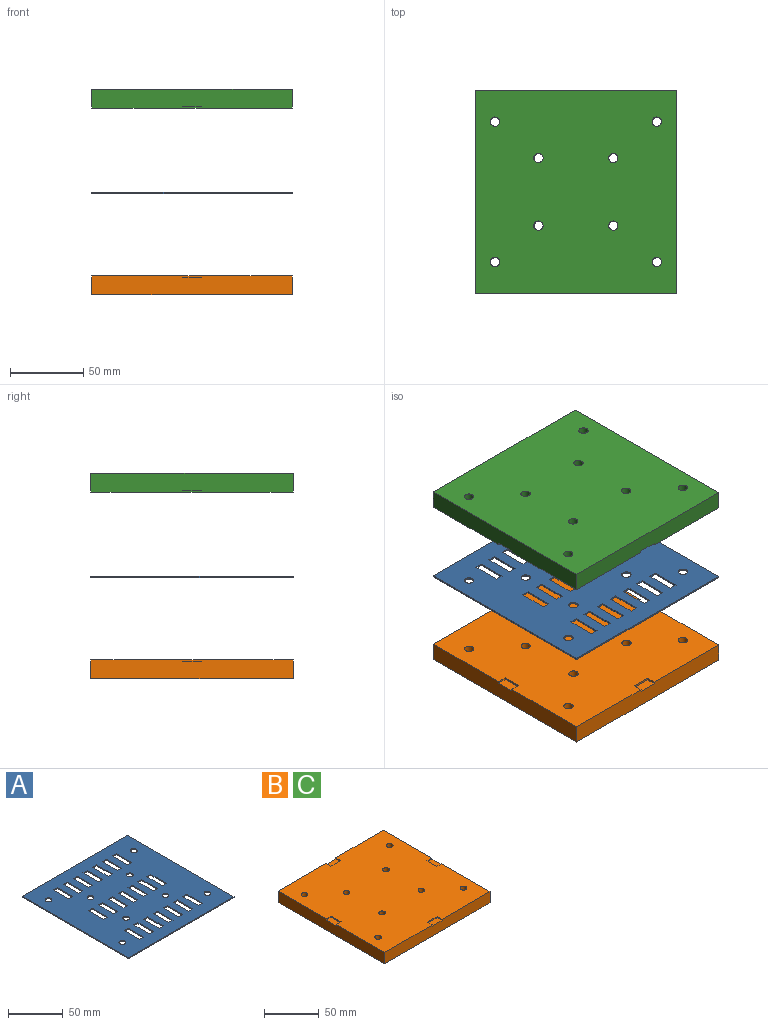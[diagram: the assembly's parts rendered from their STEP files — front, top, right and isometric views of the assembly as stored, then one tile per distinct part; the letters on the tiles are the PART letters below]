
ASSEMBLY  parts=3 mates=2
PART A: 98 faces, bbox 136.8x138x1 mm
  f0: plane 138.04x136.82mm, normal (0,0,1), area 16433.2mm2, adj f2,f3,f4,f5,f6,f7,f8,f9
  f1: plane 138.04x136.82mm, normal (0,0,-1), area 16433.2mm2, adj f2,f3,f4,f5,f6,f7,f8,f9
  f2: plane 138.04x1.02mm, normal (-1,0,0), area 140.3mm2, adj f0,f1,f3,f5
  f3: plane 136.82x1.02mm, normal (0,-1,0), area 139mm2, adj f0,f1,f2,f4
  f4: plane 138.04x1.02mm, normal (1,0,0), area 140.3mm2, adj f0,f1,f3,f5
  f5: plane 136.82x1.02mm, normal (0,1,0), area 139mm2, adj f0,f1,f2,f4
  f6: plane 5.24x1.02mm, normal (0,-1,0), area 5.3mm2, adj f0,f1,f7,f9
  f7: plane 20.02x1.02mm, normal (1,0,0), area 20.3mm2, adj f0,f1,f6,f8
  f8: plane 5.24x1.02mm, normal (0,1,0), area 5.3mm2, adj f0,f1,f7,f9
  f9: plane 20.02x1.02mm, normal (-1,0,0), area 20.3mm2, adj f0,f1,f6,f8
  f10: plane 5.24x1.02mm, normal (0,1,0), area 5.3mm2, adj f0,f1,f11,f12
  f11: plane 20.02x1.02mm, normal (1,0,0), area 20.3mm2, adj f0,f1,f10,f13
  f12: plane 20.02x1.02mm, normal (-1,0,0), area 20.3mm2, adj f0,f1,f10,f13
  f13: plane 5.24x1.02mm, normal (0,-1,0), area 5.3mm2, adj f0,f1,f11,f12
  f14: plane 5.24x1.02mm, normal (0,1,0), area 5.3mm2, adj f0,f1,f15,f16
  f15: plane 20.02x1.02mm, normal (1,0,0), area 20.3mm2, adj f0,f1,f14,f17
  f16: plane 20.02x1.02mm, normal (-1,0,0), area 20.3mm2, adj f0,f1,f14,f17
  f17: plane 5.24x1.02mm, normal (0,-1,0), area 5.3mm2, adj f0,f1,f15,f16
  f18: plane 5.24x1.02mm, normal (0,1,0), area 5.3mm2, adj f0,f1,f19,f20
  f19: plane 20.02x1.02mm, normal (1,0,0), area 20.3mm2, adj f0,f1,f18,f21
  f20: plane 20.02x1.02mm, normal (-1,0,0), area 20.3mm2, adj f0,f1,f18,f21
  f21: plane 5.24x1.02mm, normal (0,-1,0), area 5.3mm2, adj f0,f1,f19,f20
  f22: plane 5.24x1.02mm, normal (0,1,0), area 5.3mm2, adj f0,f1,f23,f24
  f23: plane 20.02x1.02mm, normal (1,0,0), area 20.3mm2, adj f0,f1,f22,f25
  f24: plane 20.02x1.02mm, normal (-1,0,0), area 20.3mm2, adj f0,f1,f22,f25
  f25: plane 5.24x1.02mm, normal (0,-1,0), area 5.3mm2, adj f0,f1,f23,f24
  f26: plane 5.24x1.02mm, normal (0,1,0), area 5.3mm2, adj f0,f1,f27,f28
  f27: plane 20.02x1.02mm, normal (1,0,0), area 20.3mm2, adj f0,f1,f26,f29
  f28: plane 20.02x1.02mm, normal (-1,0,0), area 20.3mm2, adj f0,f1,f26,f29
  f29: plane 5.24x1.02mm, normal (0,-1,0), area 5.3mm2, adj f0,f1,f27,f28
  f30: plane 20.02x1.02mm, normal (-1,0,0), area 20.3mm2, adj f0,f1,f31,f32
  f31: plane 5.24x1.02mm, normal (0,1,0), area 5.3mm2, adj f0,f1,f30,f33
  f32: plane 5.24x1.02mm, normal (0,-1,0), area 5.3mm2, adj f0,f1,f30,f33
  f33: plane 20.02x1.02mm, normal (1,0,0), area 20.3mm2, adj f0,f1,f31,f32
  f34: plane 20.02x1.02mm, normal (-1,0,0), area 20.3mm2, adj f0,f1,f35,f36
  f35: plane 5.24x1.02mm, normal (0,1,0), area 5.3mm2, adj f0,f1,f34,f37
  f36: plane 5.24x1.02mm, normal (0,-1,0), area 5.3mm2, adj f0,f1,f34,f37
  f37: plane 20.02x1.02mm, normal (1,0,0), area 20.3mm2, adj f0,f1,f35,f36
  f38: plane 5.24x1.02mm, normal (0,1,0), area 5.3mm2, adj f0,f1,f39,f40
  f39: plane 20.02x1.02mm, normal (1,0,0), area 20.3mm2, adj f0,f1,f38,f41
  f40: plane 20.02x1.02mm, normal (-1,0,0), area 20.3mm2, adj f0,f1,f38,f41
  f41: plane 5.24x1.02mm, normal (0,-1,0), area 5.3mm2, adj f0,f1,f39,f40
  f42: plane 20.02x1.02mm, normal (-1,0,0), area 20.3mm2, adj f0,f1,f43,f44
  f43: plane 5.24x1.02mm, normal (0,1,0), area 5.3mm2, adj f0,f1,f42,f45
  f44: plane 5.24x1.02mm, normal (0,-1,0), area 5.3mm2, adj f0,f1,f42,f45
  f45: plane 20.02x1.02mm, normal (1,0,0), area 20.3mm2, adj f0,f1,f43,f44
  f46: plane 20.02x1.02mm, normal (-1,0,0), area 20.3mm2, adj f0,f1,f47,f48
  f47: plane 5.24x1.02mm, normal (0,1,0), area 5.3mm2, adj f0,f1,f46,f49
  f48: plane 5.24x1.02mm, normal (0,-1,0), area 5.3mm2, adj f0,f1,f46,f49
  f49: plane 20.02x1.02mm, normal (1,0,0), area 20.3mm2, adj f0,f1,f47,f48
  f50: plane 5.24x1.02mm, normal (0,-1,0), area 5.3mm2, adj f0,f1,f51,f53
  f51: plane 20.02x1.02mm, normal (1,0,0), area 20.3mm2, adj f0,f1,f50,f52
  f52: plane 5.24x1.02mm, normal (0,1,0), area 5.3mm2, adj f0,f1,f51,f53
  f53: plane 20.02x1.02mm, normal (-1,0,0), area 20.3mm2, adj f0,f1,f50,f52
  f54: plane 5.24x1.02mm, normal (0,1,0), area 5.3mm2, adj f0,f1,f55,f56
  f55: plane 20.02x1.02mm, normal (1,0,0), area 20.3mm2, adj f0,f1,f54,f57
  f56: plane 20.02x1.02mm, normal (-1,0,0), area 20.3mm2, adj f0,f1,f54,f57
  f57: plane 5.24x1.02mm, normal (0,-1,0), area 5.3mm2, adj f0,f1,f55,f56
  f58: plane 5.24x1.02mm, normal (0,-1,0), area 5.3mm2, adj f0,f1,f59,f61
  f59: plane 20.02x1.02mm, normal (1,0,0), area 20.3mm2, adj f0,f1,f58,f60
  f60: plane 5.24x1.02mm, normal (0,1,0), area 5.3mm2, adj f0,f1,f59,f61
  f61: plane 20.02x1.02mm, normal (-1,0,0), area 20.3mm2, adj f0,f1,f58,f60
  f62: plane 5.24x1.02mm, normal (0,1,0), area 5.3mm2, adj f0,f1,f63,f64
  f63: plane 20.02x1.02mm, normal (1,0,0), area 20.3mm2, adj f0,f1,f62,f65
  f64: plane 20.02x1.02mm, normal (-1,0,0), area 20.3mm2, adj f0,f1,f62,f65
  f65: plane 5.24x1.02mm, normal (0,-1,0), area 5.3mm2, adj f0,f1,f63,f64
  f66: plane 5.24x1.02mm, normal (0,1,0), area 5.3mm2, adj f0,f1,f67,f68
  f67: plane 20.02x1.02mm, normal (1,0,0), area 20.3mm2, adj f0,f1,f66,f69
  f68: plane 20.02x1.02mm, normal (-1,0,0), area 20.3mm2, adj f0,f1,f66,f69
  f69: plane 5.24x1.02mm, normal (0,-1,0), area 5.3mm2, adj f0,f1,f67,f68
  f70: plane 5.24x1.02mm, normal (0,1,0), area 5.3mm2, adj f0,f1,f71,f72
  f71: plane 20.02x1.02mm, normal (1,0,0), area 20.3mm2, adj f0,f1,f70,f73
  f72: plane 20.02x1.02mm, normal (-1,0,0), area 20.3mm2, adj f0,f1,f70,f73
  f73: plane 5.24x1.02mm, normal (0,-1,0), area 5.3mm2, adj f0,f1,f71,f72
  f74: plane 5.24x1.02mm, normal (0,-1,0), area 5.3mm2, adj f0,f1,f75,f77
  f75: plane 20.02x1.02mm, normal (1,0,0), area 20.3mm2, adj f0,f1,f74,f76
  f76: plane 5.24x1.02mm, normal (0,1,0), area 5.3mm2, adj f0,f1,f75,f77
  f77: plane 20.02x1.02mm, normal (-1,0,0), area 20.3mm2, adj f0,f1,f74,f76
  f78: plane 5.24x1.02mm, normal (0,-1,0), area 5.3mm2, adj f0,f1,f79,f81
  f79: plane 20.02x1.02mm, normal (1,0,0), area 20.3mm2, adj f0,f1,f78,f80
  f80: plane 5.24x1.02mm, normal (0,1,0), area 5.3mm2, adj f0,f1,f79,f81
  f81: plane 20.02x1.02mm, normal (-1,0,0), area 20.3mm2, adj f0,f1,f78,f80
  f82: plane 5.24x1.02mm, normal (0,1,0), area 5.3mm2, adj f0,f1,f83,f84
  f83: plane 20.02x1.02mm, normal (1,0,0), area 20.3mm2, adj f0,f1,f82,f85
  f84: plane 20.02x1.02mm, normal (-1,0,0), area 20.3mm2, adj f0,f1,f82,f85
  f85: plane 5.24x1.02mm, normal (0,-1,0), area 5.3mm2, adj f0,f1,f83,f84
  f86: plane 5.24x1.02mm, normal (0,1,0), area 5.3mm2, adj f0,f1,f87,f88
  f87: plane 20.02x1.02mm, normal (1,0,0), area 20.3mm2, adj f0,f1,f86,f89
  f88: plane 20.02x1.02mm, normal (-1,0,0), area 20.3mm2, adj f0,f1,f86,f89
  f89: plane 5.24x1.02mm, normal (0,-1,0), area 5.3mm2, adj f0,f1,f87,f88
  f90: cylinder r=3.17mm len=6.35mm, axis (0,0,1), area 20.3mm2, adj f0,f1
  f91: cylinder r=3.17mm len=6.35mm, axis (0,0,1), area 20.3mm2, adj f0,f1
  f92: cylinder r=3.17mm len=6.35mm, axis (0,0,1), area 20.3mm2, adj f0,f1
  f93: cylinder r=3.17mm len=6.35mm, axis (0,0,1), area 20.3mm2, adj f0,f1
  f94: cylinder r=3.17mm len=6.35mm, axis (0,0,1), area 20.3mm2, adj f0,f1
  f95: cylinder r=3.17mm len=6.35mm, axis (0,0,1), area 20.3mm2, adj f0,f1
  f96: cylinder r=3.17mm len=6.35mm, axis (0,0,1), area 20.3mm2, adj f0,f1
  f97: cylinder r=3.17mm len=6.35mm, axis (0,0,1), area 20.3mm2, adj f0,f1
PART B: 30 faces, bbox 136.8x138x12.7 mm
  f0: plane 12.68x1.27mm, normal (-1,0,0), area 16.1mm2, adj f1,f15,f16,f28
  f1: plane 6.35x1.27mm, normal (0,1,0), area 8.1mm2, adj f0,f2,f16,f28
  f2: plane 138.04x12.7mm, normal (-1,0,0), area 1737.1mm2, adj f1,f3,f11,f15,f16,f17,f28
  f3: plane 136.82x12.7mm, normal (0,-1,0), area 1721.5mm2, adj f2,f4,f6,f7,f16,f17,f26
  f4: plane 6.33x1.27mm, normal (1,0,0), area 8mm2, adj f3,f5,f16,f26
  f5: plane 12.74x1.27mm, normal (0,-1,0), area 16.2mm2, adj f4,f6,f16,f26
  f6: plane 6.33x1.27mm, normal (-1,0,0), area 8mm2, adj f3,f5,f16,f26
  f7: plane 138.04x12.7mm, normal (1,0,0), area 1737.1mm2, adj f3,f8,f10,f11,f16,f17,f29
  f8: plane 6.35x1.27mm, normal (0,1,0), area 8.1mm2, adj f7,f9,f16,f29
  f9: plane 12.68x1.27mm, normal (1,0,0), area 16.1mm2, adj f8,f10,f16,f29
  f10: plane 6.35x1.27mm, normal (0,-1,0), area 8.1mm2, adj f7,f9,f16,f29
  f11: plane 136.82x12.7mm, normal (0,1,0), area 1721.5mm2, adj f2,f7,f12,f14,f16,f17,f27
  f12: plane 6.33x1.27mm, normal (-1,0,0), area 8mm2, adj f11,f13,f16,f27
  f13: plane 12.74x1.27mm, normal (0,1,0), area 16.2mm2, adj f12,f14,f16,f27
  f14: plane 6.33x1.27mm, normal (1,0,0), area 8mm2, adj f11,f13,f16,f27
  f15: plane 6.35x1.27mm, normal (0,-1,0), area 8.1mm2, adj f0,f2,f16,f28
  f16: plane 138.04x136.82mm, normal (0,0,1), area 18311.6mm2, adj f0,f1,f2,f3,f4,f5,f6,f7
  f17: plane 138.04x136.82mm, normal (0,0,-1), area 18634.1mm2, adj f2,f3,f7,f11,f18,f19,f20,f21
  f18: cylinder r=3.17mm len=12.7mm, axis (0,0,1), area 253.4mm2, adj f16,f17
  f19: cylinder r=3.17mm len=12.7mm, axis (0,0,1), area 253.4mm2, adj f16,f17
  f20: cylinder r=3.17mm len=12.7mm, axis (0,0,1), area 253.4mm2, adj f16,f17
  f21: cylinder r=3.17mm len=12.7mm, axis (0,0,1), area 253.4mm2, adj f16,f17
  f22: cylinder r=3.17mm len=12.7mm, axis (0,0,1), area 253.4mm2, adj f16,f17
  f23: cylinder r=3.17mm len=12.7mm, axis (0,0,1), area 253.4mm2, adj f16,f17
  f24: cylinder r=3.17mm len=12.7mm, axis (0,0,1), area 253.4mm2, adj f16,f17
  f25: cylinder r=3.17mm len=12.7mm, axis (0,0,1), area 253.4mm2, adj f16,f17
  f26: plane 12.74x6.33mm, normal (0,0,1), area 80.7mm2, adj f3,f4,f5,f6
  f27: plane 12.74x6.33mm, normal (0,0,1), area 80.7mm2, adj f11,f12,f13,f14
  f28: plane 12.68x6.35mm, normal (0,0,1), area 80.6mm2, adj f0,f1,f2,f15
  f29: plane 12.68x6.35mm, normal (0,0,1), area 80.6mm2, adj f7,f8,f9,f10
PART C: same geometry as B
PLACE A t=(16.46,-8.06,10.72)mm
PLACE B t=(16.49,-8.06,-58.12)mm
PLACE C rot(axis=(1,0,0),180deg) t=(16.31,-8.08,81.84)mm
MATE parallel C.f16 <-> A.f0  axis (0,0,-1) through (16.31,-8.08,69.14)mm
MATE parallel A.f0 <-> B.f16  axis (0,0,1) through (16.49,-8.06,11.73)mm
